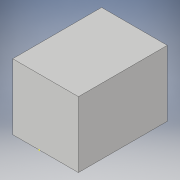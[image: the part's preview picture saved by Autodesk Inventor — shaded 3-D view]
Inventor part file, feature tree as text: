
AUTODESK INVENTOR PART (.ipt)
format: ipt  version: 2019 (Build 230136000, 136)  size: 101,376 bytes
history: native  units: mm
features: sketch x3, other x1, extrude x1, hole x1
ambient origin geometry x8: Origin, YZ Plane, XZ Plane, XY Plane, X Axis, Y Axis, Z Axis, Center Point
bodies: Body1 (feature_tree)
feature tree (6):
  other  "ソリッド1"
  extrude  "押し出し1"  Depth=20.0mm
  sketch  "スケッチ2"
  hole  "穴1"  [1 undecoded]
  sketch  "スケッチ1"
  sketch  "スケッチ3"
note: 1 required parameter value undecoded (feature->parameter linkage not recoverable at this tier; creation-order binding heuristic only, values carry confidence <= 0.55)
